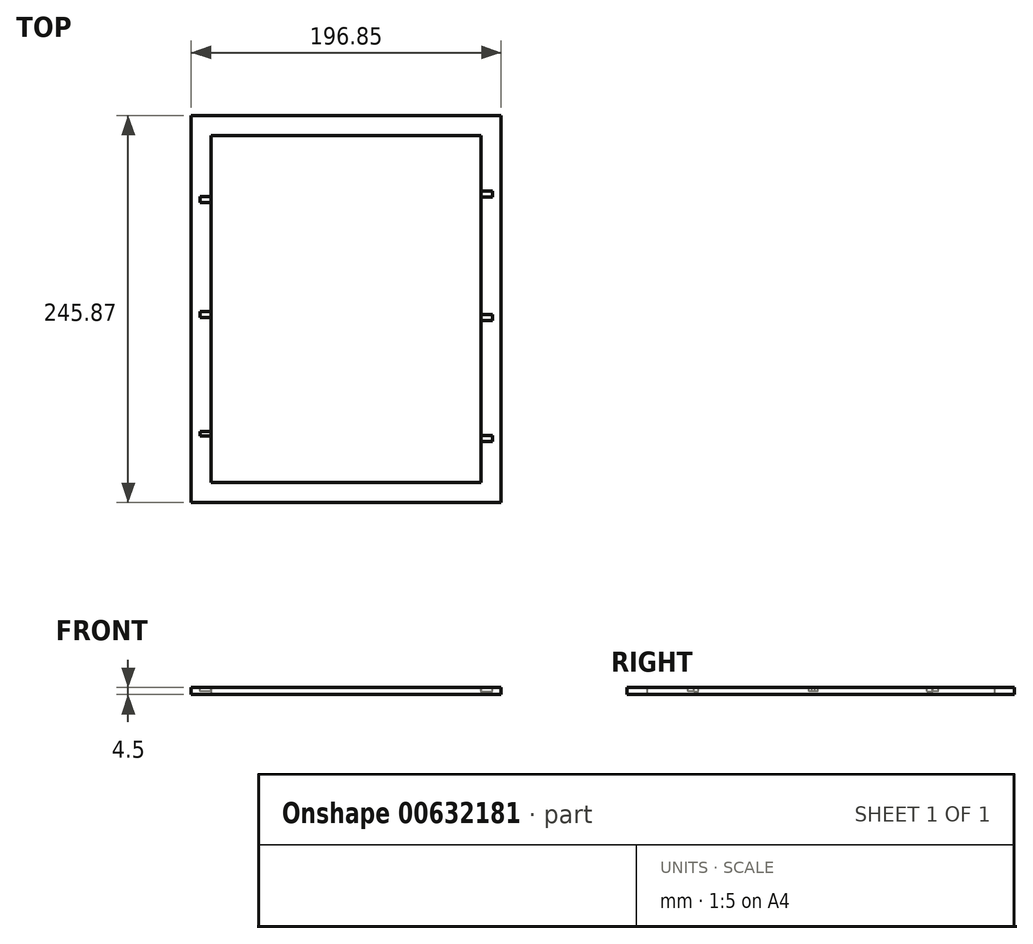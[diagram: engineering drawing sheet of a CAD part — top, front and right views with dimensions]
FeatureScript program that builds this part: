
annotation { "Feature Type Name" : "Feature", "Feature Type Description" : "" }
export const myFeature = defineFeature(function(context is Context, id is Id, definition is map)
    precondition{}
    {
        {
            var Q0;
            Q0=qCreatedBy(makeId("Top.planeOp"),FACE);
            var sketch = newSketch(context, id + "F0", { "sketchPlane" : qUnion([Q0])});
            skLineSegment(sketch, "E0.bottom", {"start": v(-98.45, 143.07) * mm, "end": v(98.4, 143.07) * mm});
            skLineSegment(sketch, "E0.top", {"start": v(-98.45, -102.8) * mm, "end": v(98.4, -102.8) * mm});
            skLineSegment(sketch, "E0.left", {"start": v(-98.45, 143.07) * mm, "end": v(-98.45, -102.8) * mm});
            skLineSegment(sketch, "E0.right", {"start": v(98.4, 143.07) * mm, "end": v(98.4, -102.8) * mm});
            skLineSegment(sketch, "E1.bottom", {"start": v(85.7, -90.1) * mm, "end": v(-85.75, -90.1) * mm});
            skLineSegment(sketch, "E1.top", {"start": v(85.7, 130.37) * mm, "end": v(-85.75, 130.37) * mm});
            skLineSegment(sketch, "E1.left", {"start": v(85.7, -90.1) * mm, "end": v(85.7, 130.37) * mm});
            skLineSegment(sketch, "E1.right", {"start": v(-85.75, -90.1) * mm, "end": v(-85.75, 130.37) * mm});
            skSolve(sketch);
        }
        {
            var Q0;
            Q0=makeQuery(id+"F0.imprint","IMPRINT",FACE,{"disambiguationData":[TD([[makeQuery(id+"F0.imprint","IMPRINT",EDGE,{"derivedFrom":sQuery(id+"F0.wireOp",EDGE,"E1.bottom")}),-1.0]])]});
            var Q1;
            Q1=makeQuery(id+"F0.imprint","IMPRINT",FACE,{"disambiguationData":[TD([[makeQuery(id+"F0.imprint","IMPRINT",EDGE,{"derivedFrom":sQuery(id+"F0.wireOp",EDGE,"E0.bottom")}),-1.0]])]});
            var Q2;
            Q2=sQuery(id+"F0.wireOp",EDGE,"E0.bottom");
            var Q3;
            Q3=sQuery(id+"F0.wireOp",EDGE,"E0.left");
            var Q4;
            Q4=sQuery(id+"F0.wireOp",EDGE,"E0.right");
            var Q5;
            Q5=sQuery(id+"F0.wireOp",EDGE,"E0.top");
            extrude(context, id + "F1", {"entities" : qUnion([Q0, Q1]), "surfaceEntities" : qUnion([Q2, Q3, Q4, Q5]), "depth" : 4.5 * mm, "offsetDistance" : 25.4 * mm});
        }
        {
            var Q0;
            Q0=makeQuery(id+"F0.imprint","IMPRINT",FACE,{"disambiguationData":[TD([[makeQuery(id+"F0.imprint","IMPRINT",EDGE,{"derivedFrom":sQuery(id+"F0.wireOp",EDGE,"E1.bottom")}),-1.0]])]});
            extrude(context, id + "F2", {"entities" : qUnion([Q0]), "operationType" : NewBodyOperationType.REMOVE, "depth" : 4.5 * mm, "offsetDistance" : 25.4 * mm});
        }
        {
            var Q0;
            Q0=makeQuery(id+"F1.opExtrude","CAP_FACE",FACE,{"disambiguationData":[OSD([sQuery(id+"F0.wireOp",EDGE,"E0.bottom"),sQuery(id+"F0.wireOp",EDGE,"E0.top"),sQuery(id+"F0.wireOp",EDGE,"E0.left"),sQuery(id+"F0.wireOp",EDGE,"E0.right")])],"isStart":false});
            var sketch = newSketch(context, id + "F3", { "sketchPlane" : qUnion([Q0])});
            skLineSegment(sketch, "E2.bottom", {"start": v(-85.75, 87.76) * mm, "end": v(-92.86, 87.76) * mm});
            skLineSegment(sketch, "E2.top", {"start": v(-85.75, 91.57) * mm, "end": v(-92.86, 91.57) * mm});
            skLineSegment(sketch, "E2.left", {"start": v(-85.75, 87.76) * mm, "end": v(-85.75, 91.57) * mm});
            skLineSegment(sketch, "E2.right", {"start": v(-92.86, 87.76) * mm, "end": v(-92.86, 91.57) * mm});
            skSolve(sketch);
        }
        {
            var Q0;
            Q0 = qSketchRegion(id + "F3", true);
            extrude(context, id + "F4", {"entities" : qUnion([Q0]), "operationType" : NewBodyOperationType.REMOVE, "oppositeDirection" : true, "depth" : 2.54 * mm, "offsetDistance" : 25.4 * mm});
        }
        {
            var Q0;
            {var subQ2=sQuery(id+"F3.wireOp",EDGE,"E2.bottom");Q0=makeQuery(id+"F3.imprint","IMPRINT",FACE,{"disambiguationData":[TD([[makeQuery(id+"F3.imprint","IMPRINT",EDGE,{"derivedFrom":subQ2}),1.0]])]});}
            var sketch = newSketch(context, id + "F5", { "sketchPlane" : qUnion([Q0])});
            skLineSegment(sketch, "E3.bottom", {"start": v(-85.75, -60.46) * mm, "end": v(-92.86, -60.46) * mm});
            skLineSegment(sketch, "E3.top", {"start": v(-85.75, -57.57) * mm, "end": v(-92.86, -57.57) * mm});
            skLineSegment(sketch, "E3.left", {"start": v(-85.75, -60.46) * mm, "end": v(-85.75, -57.57) * mm});
            skLineSegment(sketch, "E3.right", {"start": v(-92.86, -60.46) * mm, "end": v(-92.86, -57.57) * mm});
            skSolve(sketch);
        }
        {
            var Q0;
            {var subQ0=sQuery(id+"F5.wireOp",EDGE,"E3.right");Q0=makeQuery(id+"F5.imprint","IMPRINT",FACE,{"disambiguationData":[TD([[makeQuery(id+"F5.imprint","IMPRINT",EDGE,{"derivedFrom":subQ0}),-1.0]])]});}
            extrude(context, id + "F6", {"entities" : qUnion([Q0]), "operationType" : NewBodyOperationType.REMOVE, "oppositeDirection" : true, "depth" : 2.54 * mm, "offsetDistance" : 25.4 * mm});
        }
        {
            var Q0;
            {var subQ2=sQuery(id+"F3.wireOp",EDGE,"E2.bottom");Q0=makeQuery(id+"F3.imprint","IMPRINT",FACE,{"disambiguationData":[TD([[makeQuery(id+"F3.imprint","IMPRINT",EDGE,{"derivedFrom":subQ2}),1.0]])]});}
            var sketch = newSketch(context, id + "F7", { "sketchPlane" : qUnion([Q0])});
            skLineSegment(sketch, "E4.bottom", {"start": v(85.7, 94.91) * mm, "end": v(92.8, 94.91) * mm});
            skLineSegment(sketch, "E4.top", {"start": v(85.7, 91.1) * mm, "end": v(92.8, 91.1) * mm});
            skLineSegment(sketch, "E4.left", {"start": v(85.7, 94.91) * mm, "end": v(85.7, 91.1) * mm});
            skLineSegment(sketch, "E4.right", {"start": v(92.8, 94.91) * mm, "end": v(92.8, 91.1) * mm});
            skSolve(sketch);
        }
        {
            var Q0;
            Q0 = qSketchRegion(id + "F7", true);
            extrude(context, id + "F8", {"entities" : qUnion([Q0]), "operationType" : NewBodyOperationType.REMOVE, "oppositeDirection" : true, "depth" : 2.54 * mm, "offsetDistance" : 25.4 * mm});
        }
        {
            var Q0;
            {var subQ2=sQuery(id+"F3.wireOp",EDGE,"E2.bottom");Q0=makeQuery(id+"F3.imprint","IMPRINT",FACE,{"disambiguationData":[TD([[makeQuery(id+"F3.imprint","IMPRINT",EDGE,{"derivedFrom":subQ2}),1.0]])]});}
            var sketch = newSketch(context, id + "F9", { "sketchPlane" : qUnion([Q0])});
            skLineSegment(sketch, "E5.bottom", {"start": v(85.69, -64.13) * mm, "end": v(92.8, -64.13) * mm});
            skLineSegment(sketch, "E5.top", {"start": v(85.69, -60.32) * mm, "end": v(92.8, -60.32) * mm});
            skLineSegment(sketch, "E5.left", {"start": v(85.69, -64.13) * mm, "end": v(85.69, -60.32) * mm});
            skLineSegment(sketch, "E5.right", {"start": v(92.8, -64.13) * mm, "end": v(92.8, -60.32) * mm});
            skSolve(sketch);
        }
        {
            var Q0;
            Q0 = qSketchRegion(id + "F9", true);
            extrude(context, id + "F10", {"entities" : qUnion([Q0]), "operationType" : NewBodyOperationType.REMOVE, "oppositeDirection" : true, "depth" : 2.54 * mm, "offsetDistance" : 25.4 * mm});
        }
        {
            var Q0;
            {var subQ2=sQuery(id+"F3.wireOp",EDGE,"E2.bottom");Q0=makeQuery(id+"F3.imprint","IMPRINT",FACE,{"disambiguationData":[TD([[makeQuery(id+"F3.imprint","IMPRINT",EDGE,{"derivedFrom":subQ2}),1.0]])]});}
            var sketch = newSketch(context, id + "F11", { "sketchPlane" : qUnion([Q0])});
            skLineSegment(sketch, "E6.bottom", {"start": v(85.7, 16.54) * mm, "end": v(92.82, 16.54) * mm});
            skLineSegment(sketch, "E6.top", {"start": v(85.7, 12.73) * mm, "end": v(92.82, 12.73) * mm});
            skLineSegment(sketch, "E6.left", {"start": v(85.7, 16.54) * mm, "end": v(85.7, 12.73) * mm});
            skLineSegment(sketch, "E6.right", {"start": v(92.82, 16.54) * mm, "end": v(92.82, 12.73) * mm});
            skSolve(sketch);
        }
        {
            var Q0;
            Q0 = qSketchRegion(id + "F11", true);
            extrude(context, id + "F12", {"entities" : qUnion([Q0]), "operationType" : NewBodyOperationType.REMOVE, "oppositeDirection" : true, "depth" : 2.54 * mm, "offsetDistance" : 25.4 * mm});
        }
        {
            var Q0;
            {var subQ2=sQuery(id+"F3.wireOp",EDGE,"E2.bottom");Q0=makeQuery(id+"F3.imprint","IMPRINT",FACE,{"disambiguationData":[TD([[makeQuery(id+"F3.imprint","IMPRINT",EDGE,{"derivedFrom":subQ2}),1.0]])]});}
            var sketch = newSketch(context, id + "F13", { "sketchPlane" : qUnion([Q0])});
            skLineSegment(sketch, "E7.bottom", {"start": v(-85.75, 18.42) * mm, "end": v(-92.86, 18.42) * mm});
            skLineSegment(sketch, "E7.top", {"start": v(-85.75, 14.61) * mm, "end": v(-92.86, 14.61) * mm});
            skLineSegment(sketch, "E7.left", {"start": v(-85.75, 18.42) * mm, "end": v(-85.75, 14.61) * mm});
            skLineSegment(sketch, "E7.right", {"start": v(-92.86, 18.42) * mm, "end": v(-92.86, 14.61) * mm});
            skSolve(sketch);
        }
        {
            var Q0;
            Q0 = qSketchRegion(id + "F13", true);
            extrude(context, id + "F14", {"entities" : qUnion([Q0]), "operationType" : NewBodyOperationType.REMOVE, "oppositeDirection" : true, "depth" : 2.54 * mm, "offsetDistance" : 25.4 * mm});
        }
    });
